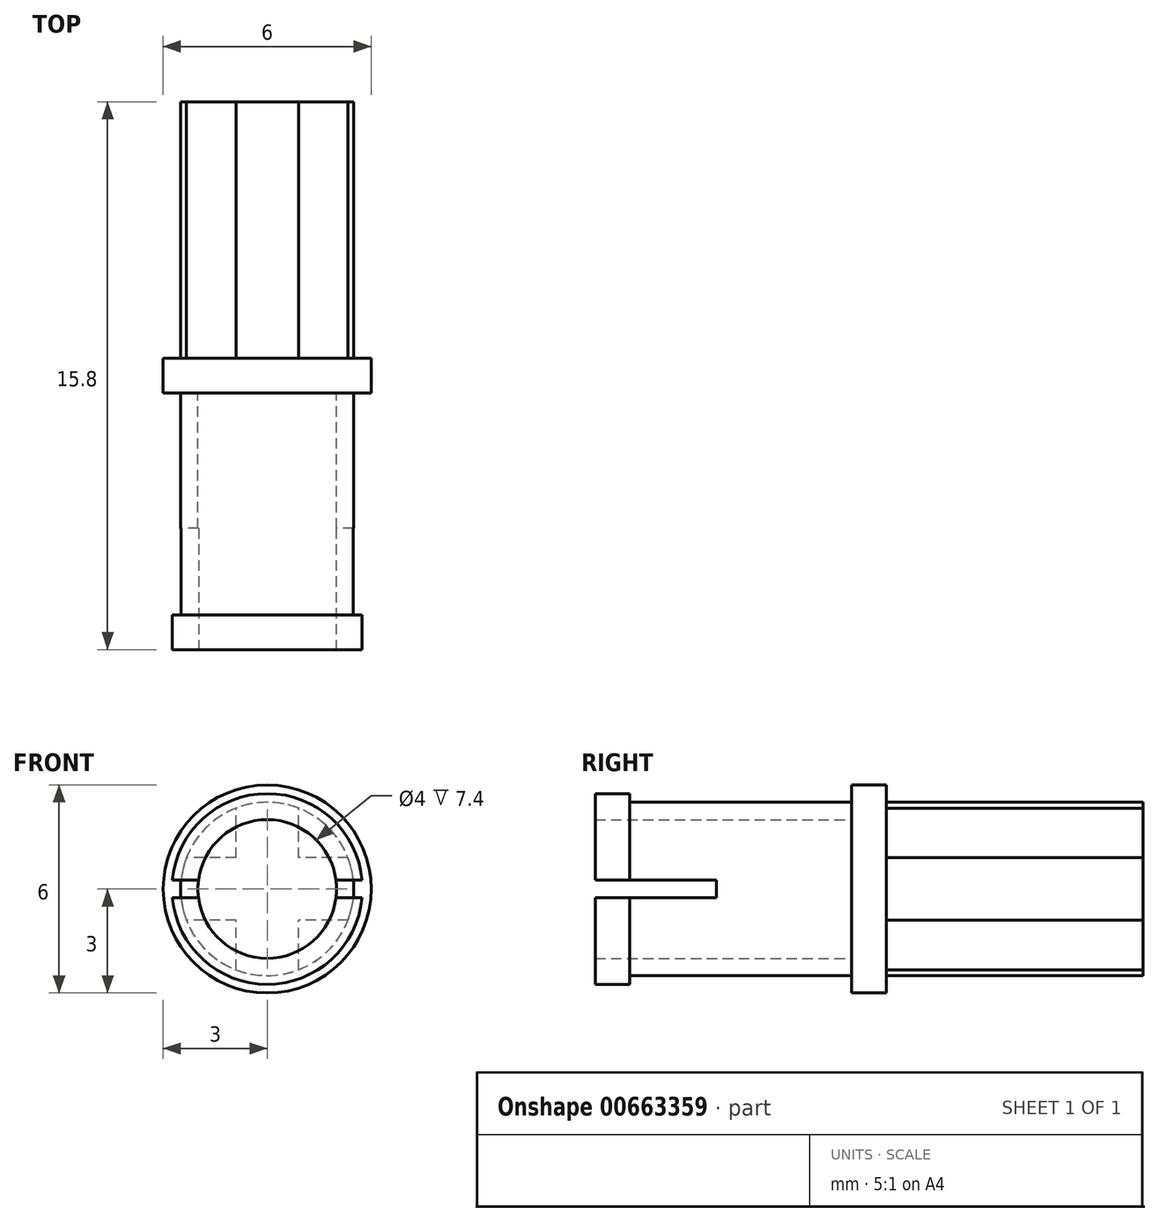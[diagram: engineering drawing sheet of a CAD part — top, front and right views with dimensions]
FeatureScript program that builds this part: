
annotation { "Feature Type Name" : "Feature", "Feature Type Description" : "" }
export const myFeature = defineFeature(function(context is Context, id is Id, definition is map)
    precondition{}
    {
        {
            var Q0;
            Q0=qCreatedBy(makeId("Front.planeOp"),FACE);
            var sketch = newSketch(context, id + "F0", { "sketchPlane" : qUnion([Q0])});
            skCircle(sketch, "E0", {"center": v(0, 0) * mm, "radius": 3 * mm});
            skSolve(sketch);
        }
        {
            var Q0;
            Q0=qSketchRegion(id+"F0",true);
            extrude(context, id + "F1", {"entities" : qUnion([Q0]), "endBound" : BoundingType.SYMMETRIC, "depth" : 1 * mm, "offsetDistance" : 25 * mm});
        }
        {
            var Q0;
            Q0=makeQuery(id+"F1.opExtrude","CAP_FACE",FACE,{"disambiguationData":[OSD([sQuery(id+"F0.wireOp",EDGE,"E0")])],"isStart":false});
            var sketch = newSketch(context, id + "F2", { "sketchPlane" : qUnion([Q0])});
            skCircle(sketch, "E1", {"center": v(0, 0) * mm, "radius": 2.5 * mm});
            skCircle(sketch, "E2", {"center": v(0, 0) * mm, "radius": 2 * mm});
            skSolve(sketch);
        }
        {
            var Q0;
            Q0=makeQuery(id+"F2.imprint","IMPRINT",FACE,{"disambiguationData":[TD([[makeQuery(id+"F2.imprint","IMPRINT",EDGE,{"derivedFrom":sQuery(id+"F2.wireOp",EDGE,"E1")}),1.0]])]});
            extrude(context, id + "F3", {"entities" : qUnion([Q0]), "operationType" : NewBodyOperationType.ADD, "depth" : 5.9 * mm, "offsetDistance" : 25 * mm});
        }
        {
            var Q0;
            Q0=makeQuery(id+"F3.opExtrude","CAP_FACE",FACE,{"disambiguationData":[OSD([sQuery(id+"F2.wireOp",EDGE,"E1"),sQuery(id+"F2.wireOp",EDGE,"E2")])],"isStart":false});
            var sketch = newSketch(context, id + "F4", { "sketchPlane" : qUnion([Q0])});
            skCircle(sketch, "E3", {"center": v(0, 0) * mm, "radius": 2.75 * mm});
            skCircle(sketch, "E4", {"center": v(0, 0) * mm, "radius": 2 * mm});
            skSolve(sketch);
        }
        {
            var Q0;
            Q0=qSketchRegion(id+"F4",true);
            extrude(context, id + "F5", {"entities" : qUnion([Q0]), "operationType" : NewBodyOperationType.ADD, "depth" : 1 * mm, "offsetDistance" : 25 * mm});
        }
        {
            var Q0;
            Q0=makeQuery(id+"F5.opExtrude","CAP_FACE",FACE,{"disambiguationData":[OSD([sQuery(id+"F4.wireOp",EDGE,"E3"),sQuery(id+"F4.wireOp",EDGE,"E4")])],"isStart":false});
            var sketch = newSketch(context, id + "F6", { "sketchPlane" : qUnion([Q0])});
            skLineSegment(sketch, "E5.bottom", {"start": v(2.74, 0.25) * mm, "end": v(1.98, 0.25) * mm});
            skLineSegment(sketch, "E5.top", {"start": v(2.74, -0.25) * mm, "end": v(1.98, -0.25) * mm});
            skPoint(sketch, "E5.middle", {"position": v(0, 0) * mm});
            skArc(sketch, "E6.0", {"start": v(1.98, -0.25) * mm, "mid": v(2, 0) * mm, "end": v(1.98, 0.25) * mm});
            skArc(sketch, "E7.0", {"start": v(2.74, -0.25) * mm, "mid": v(2.75, 0) * mm, "end": v(2.74, 0.25) * mm});
            skPoint(sketch, "E5.right.start.orphan", {"position": v(-3.56, 0.25) * mm});
            skPoint(sketch, "E8.orphan", {"position": v(-3.56, -0.25) * mm});
            skLineSegment(sketch, "E9.trimOffspring", {"start": v(-1.98, -0.25) * mm, "end": v(-2.74, -0.25) * mm});
            skLineSegment(sketch, "E10.trimOffspring", {"start": v(-1.98, 0.25) * mm, "end": v(-2.74, 0.25) * mm});
            skArc(sketch, "E11.trimOffspring", {"start": v(-1.98, 0.25) * mm, "mid": v(-2, 0) * mm, "end": v(-1.98, -0.25) * mm});
            skArc(sketch, "E12.trimOffspring", {"start": v(-2.74, 0.25) * mm, "mid": v(-2.75, 0) * mm, "end": v(-2.74, -0.25) * mm});
            skPoint(sketch, "E5.left.start.orphan", {"position": v(3.56, 0.25) * mm});
            skPoint(sketch, "E13.orphan", {"position": v(3.56, -0.25) * mm});
            skSolve(sketch);
        }
        {
            var Q0;
            Q0=qSketchRegion(id+"F6",true);
            extrude(context, id + "F7", {"entities" : qUnion([Q0]), "operationType" : NewBodyOperationType.REMOVE, "oppositeDirection" : true, "depth" : 3 * mm, "offsetDistance" : 25 * mm});
        }
        {
            var Q0;
            Q0=makeQuery(id+"F1.opExtrude","CAP_FACE",FACE,{"disambiguationData":[OSD([sQuery(id+"F0.wireOp",EDGE,"E0")])],"isStart":true});
            var sketch = newSketch(context, id + "F8", { "sketchPlane" : qUnion([Q0])});
            skArc(sketch, "E14", {"start": v(-0.9, -2.33) * mm, "mid": v(0, -2.5) * mm, "end": v(0.9, -2.33) * mm});
            skLineSegment(sketch, "E15.bottom", {"start": v(-2.33, 0.9) * mm, "end": v(-0.9, 0.9) * mm});
            skLineSegment(sketch, "E15.top", {"start": v(-2.33, -0.9) * mm, "end": v(-0.9, -0.9) * mm});
            skLineSegment(sketch, "E16.left", {"start": v(0.9, -2.33) * mm, "end": v(0.9, -0.9) * mm});
            skLineSegment(sketch, "E16.right", {"start": v(-0.9, -2.33) * mm, "end": v(-0.9, -0.9) * mm});
            skPoint(sketch, "E16.bottom.start.orphan", {"position": v(0.9, -3.65) * mm});
            skPoint(sketch, "E17.orphan", {"position": v(-0.9, -3.65) * mm});
            skPoint(sketch, "E15.left.end.orphan", {"position": v(-3.38, -0.9) * mm});
            skPoint(sketch, "E18.orphan", {"position": v(-3.38, 0.9) * mm});
            skPoint(sketch, "E19.orphan", {"position": v(0.9, 3.65) * mm});
            skPoint(sketch, "E20.orphan", {"position": v(-0.9, 3.65) * mm});
            skPoint(sketch, "E15.right.start.orphan", {"position": v(3.38, 0.9) * mm});
            skPoint(sketch, "E21.orphan", {"position": v(3.38, -0.9) * mm});
            skArc(sketch, "E22.trimOffspring", {"start": v(-2.33, 0.9) * mm, "mid": v(-2.5, 0) * mm, "end": v(-2.33, -0.9) * mm});
            skArc(sketch, "E23.trimOffspring", {"start": v(2.33, -0.9) * mm, "mid": v(2.5, 0) * mm, "end": v(2.33, 0.9) * mm});
            skArc(sketch, "E24.trimOffspring", {"start": v(0.9, 2.33) * mm, "mid": v(0, 2.5) * mm, "end": v(-0.9, 2.33) * mm});
            skLineSegment(sketch, "E25.trimOffspring", {"start": v(-0.9, 0.9) * mm, "end": v(-0.9, 2.33) * mm});
            skLineSegment(sketch, "E26.trimOffspring", {"start": v(0.9, 0.9) * mm, "end": v(0.9, 2.33) * mm});
            skLineSegment(sketch, "E27.trimOffspring", {"start": v(0.9, -0.9) * mm, "end": v(2.33, -0.9) * mm});
            skLineSegment(sketch, "E28.trimOffspring", {"start": v(0.9, 0.9) * mm, "end": v(2.33, 0.9) * mm});
            skSolve(sketch);
        }
        {
            var Q0;
            Q0=makeQuery(id+"F8.imprint","IMPRINT",FACE,{"disambiguationData":[TD([[makeQuery(id+"F8.imprint","IMPRINT",EDGE,{"derivedFrom":sQuery(id+"F8.wireOp",EDGE,"E14")}),1.0]])]});
            extrude(context, id + "F9", {"entities" : qUnion([Q0]), "operationType" : NewBodyOperationType.ADD, "depth" : 7.4 * mm, "offsetDistance" : 25 * mm});
        }
        {
            var Q0;
            {var subQ0=sQuery(id+"F4.wireOp",EDGE,"E4");var subQ1=sQuery(id+"F4.wireOp",EDGE,"E3");Q0=makeQuery(id+"F7.boolean.opBoolean","SPLIT",FACE,{"disambiguationData":[TD([makeQuery(id+"F7.opExtrude","SWEPT_FACE",FACE,{"disambiguationData":[OSD([sQuery(id+"F6.wireOp",EDGE,"E5.bottom")])]})])],"derivedFrom":makeQuery(id+"F5.opExtrude","CAP_FACE",FACE,{"disambiguationData":[OSD([subQ1,subQ0])],"isStart":false})});}
            var Q1;
            {var subQ0=sQuery(id+"F4.wireOp",EDGE,"E4");var subQ1=sQuery(id+"F4.wireOp",EDGE,"E3");Q1=makeQuery(id+"F7.boolean.opBoolean","SPLIT",FACE,{"disambiguationData":[TD([makeQuery(id+"F7.opExtrude","SWEPT_FACE",FACE,{"disambiguationData":[OSD([sQuery(id+"F6.wireOp",EDGE,"E5.top")])]})])],"derivedFrom":makeQuery(id+"F5.opExtrude","CAP_FACE",FACE,{"disambiguationData":[OSD([subQ1,subQ0])],"isStart":false})});}
            extrude(context, id + "F10", {"entities" : qUnion([Q0, Q1]), "operationType" : NewBodyOperationType.ADD, "depth" : 0.5 * mm, "offsetDistance" : 25 * mm});
        }
        {
            var Q0;
            {var subQ0=sQuery(id+"F4.wireOp",EDGE,"E3");Q0=makeQuery(id+"F7.boolean.opBoolean","SPLIT",FACE,{"disambiguationData":[TD([makeQuery(id+"F7.opExtrude","SWEPT_FACE",FACE,{"disambiguationData":[OSD([sQuery(id+"F6.wireOp",EDGE,"E5.bottom")])]})])],"derivedFrom":makeQuery(id+"F5.opExtrude","CAP_FACE",FACE,{"disambiguationData":[OSD([subQ0,sQuery(id+"F4.wireOp",EDGE,"E4")])],"isStart":true})});}
            var Q1;
            {var subQ0=sQuery(id+"F4.wireOp",EDGE,"E3");Q1=makeQuery(id+"F7.boolean.opBoolean","SPLIT",FACE,{"disambiguationData":[TD([makeQuery(id+"F7.opExtrude","SWEPT_FACE",FACE,{"disambiguationData":[OSD([sQuery(id+"F6.wireOp",EDGE,"E5.top")])]})])],"derivedFrom":makeQuery(id+"F5.opExtrude","CAP_FACE",FACE,{"disambiguationData":[OSD([subQ0,sQuery(id+"F4.wireOp",EDGE,"E4")])],"isStart":true})});}
            extrude(context, id + "F11", {"entities" : qUnion([Q0, Q1]), "operationType" : NewBodyOperationType.REMOVE, "oppositeDirection" : true, "depth" : 0.5 * mm, "offsetDistance" : 25 * mm});
        }
    });
